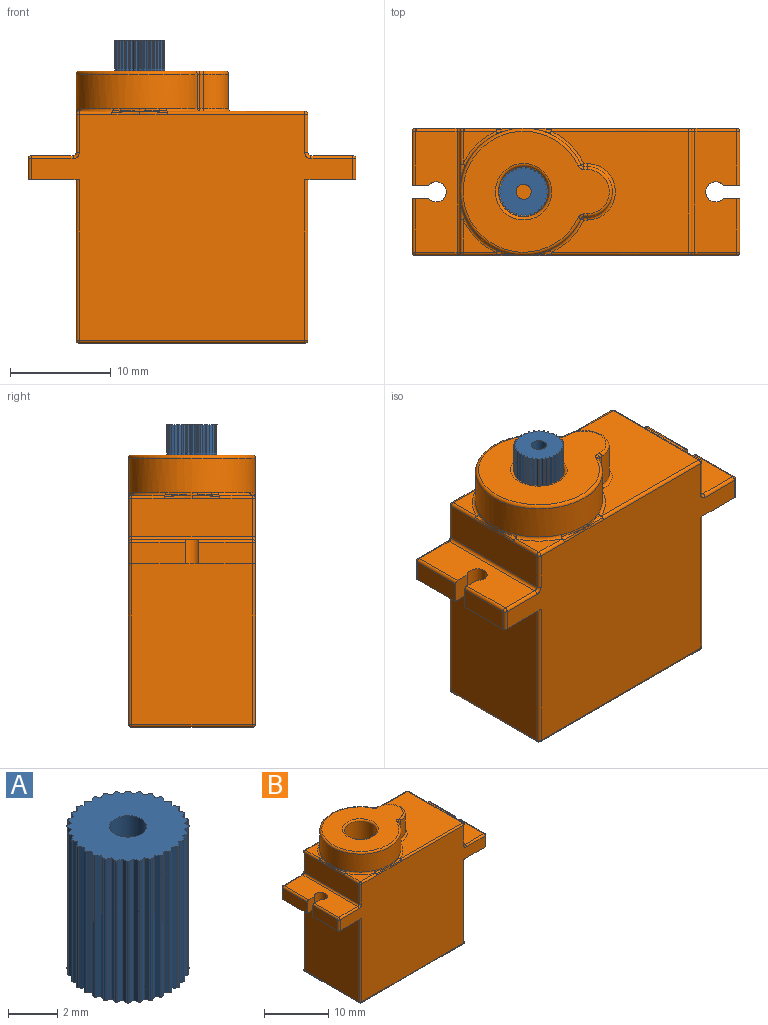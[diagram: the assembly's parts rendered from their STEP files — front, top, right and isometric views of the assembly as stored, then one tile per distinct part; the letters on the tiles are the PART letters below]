
ASSEMBLY  parts=2 mates=1
PART A: 99 faces, bbox 5x5x7 mm
  f0: plane 4.96x4.96mm, normal (0,0,1), area 16.3mm2, adj f1,f2,f3,f4,f5,f6,f7,f8
  f1: plane 7x0.22mm, normal (-0.39,0.92,0), area 1.7mm2, adj f0,f2,f94,f95
  f2: cylinder r=0.08mm len=7mm, axis (0,0,-1), area 0.9mm2, adj f0,f1,f3,f95
  f3: plane 7x0.22mm, normal (-0.93,-0.38,0), area 1.7mm2, adj f0,f2,f4,f95
  f4: plane 7x0.2mm, normal (-0.56,0.83,0), area 1.7mm2, adj f0,f3,f5,f95
  f5: cylinder r=0.08mm len=7mm, axis (0,0,-1), area 0.9mm2, adj f0,f4,f6,f95
  f6: plane 7x0.2mm, normal (-0.83,-0.55,0), area 1.7mm2, adj f0,f5,f7,f95
  f7: plane 7x0.17mm, normal (-0.71,0.7,0), area 1.7mm2, adj f0,f6,f8,f95
  f8: cylinder r=0.08mm len=7mm, axis (0,0,-1), area 0.9mm2, adj f0,f7,f9,f95
  f9: plane 7x0.17mm, normal (-0.71,-0.7,0), area 1.7mm2, adj f0,f8,f10,f95
  f10: plane 7x0.2mm, normal (-0.83,0.55,0), area 1.7mm2, adj f0,f9,f11,f95
  f11: cylinder r=0.08mm len=7mm, axis (0,0,-1), area 0.9mm2, adj f0,f10,f12,f95
  f12: plane 7x0.2mm, normal (-0.56,-0.83,0), area 1.7mm2, adj f0,f11,f13,f95
  f13: plane 7x0.22mm, normal (-0.93,0.38,0), area 1.7mm2, adj f0,f12,f14,f95
  f14: cylinder r=0.08mm len=7mm, axis (0,0,-1), area 0.9mm2, adj f0,f13,f15,f95
  f15: plane 7x0.22mm, normal (-0.39,-0.92,0), area 1.7mm2, adj f0,f14,f16,f95
  f16: plane 7x0.23mm, normal (-0.98,0.19,0), area 1.7mm2, adj f0,f15,f17,f95
  f17: cylinder r=0.08mm len=7mm, axis (0,0,-1), area 0.9mm2, adj f0,f16,f18,f95
  f18: plane 7x0.23mm, normal (-0.2,-0.98,0), area 1.7mm2, adj f0,f17,f19,f95
  f19: plane 7x0.24mm, normal (-1,0,0), area 1.7mm2, adj f0,f18,f20,f95
  f20: cylinder r=0.08mm len=7mm, axis (0,0,-1), area 0.9mm2, adj f0,f19,f21,f95
  f21: plane 7x0.24mm, normal (0,-1,0), area 1.7mm2, adj f0,f20,f22,f95
  f22: plane 7x0.23mm, normal (-0.98,-0.2,0), area 1.7mm2, adj f0,f21,f23,f95
  f23: cylinder r=0.08mm len=7mm, axis (0,0,-1), area 0.9mm2, adj f0,f22,f24,f95
  f24: plane 7x0.23mm, normal (0.19,-0.98,0), area 1.7mm2, adj f0,f23,f25,f95
  f25: plane 7x0.22mm, normal (-0.92,-0.39,0), area 1.7mm2, adj f0,f24,f26,f95
  f26: cylinder r=0.08mm len=7mm, axis (0,0,-1), area 0.9mm2, adj f0,f25,f27,f95
  f27: plane 7x0.22mm, normal (0.38,-0.93,0), area 1.7mm2, adj f0,f26,f28,f95
  f28: plane 7x0.2mm, normal (-0.83,-0.56,0), area 1.7mm2, adj f0,f27,f29,f95
  f29: cylinder r=0.08mm len=7mm, axis (0,0,-1), area 0.9mm2, adj f0,f28,f30,f95
  f30: plane 7x0.2mm, normal (0.55,-0.83,0), area 1.7mm2, adj f0,f29,f31,f95
  f31: plane 7x0.17mm, normal (-0.7,-0.71,0), area 1.7mm2, adj f0,f30,f32,f95
  f32: cylinder r=0.08mm len=7mm, axis (0,0,-1), area 0.9mm2, adj f0,f31,f33,f95
  f33: plane 7x0.17mm, normal (0.7,-0.71,0), area 1.7mm2, adj f0,f32,f34,f95
  f34: plane 7x0.2mm, normal (-0.55,-0.83,0), area 1.7mm2, adj f0,f33,f35,f95
  f35: cylinder r=0.08mm len=7mm, axis (0,0,-1), area 0.9mm2, adj f0,f34,f36,f95
  f36: plane 7x0.2mm, normal (0.83,-0.56,0), area 1.7mm2, adj f0,f35,f37,f95
  f37: plane 7x0.22mm, normal (-0.38,-0.93,0), area 1.7mm2, adj f0,f36,f38,f95
  f38: cylinder r=0.08mm len=7mm, axis (0,0,-1), area 0.9mm2, adj f0,f37,f39,f95
  f39: plane 7x0.22mm, normal (0.92,-0.39,0), area 1.7mm2, adj f0,f38,f40,f95
  f40: plane 7x0.23mm, normal (-0.19,-0.98,0), area 1.7mm2, adj f0,f39,f41,f95
  f41: cylinder r=0.08mm len=7mm, axis (0,0,-1), area 0.9mm2, adj f0,f40,f42,f95
  f42: plane 7x0.23mm, normal (0.98,-0.2,0), area 1.7mm2, adj f0,f41,f43,f95
  f43: plane 7x0.24mm, normal (0,-1,0), area 1.7mm2, adj f0,f42,f44,f95
  f44: cylinder r=0.08mm len=7mm, axis (0,0,-1), area 0.9mm2, adj f0,f43,f45,f95
  f45: plane 7x0.24mm, normal (1,0,0), area 1.7mm2, adj f0,f44,f46,f95
  f46: plane 7x0.23mm, normal (0.2,-0.98,0), area 1.7mm2, adj f0,f45,f47,f95
  f47: cylinder r=0.08mm len=7mm, axis (0,0,-1), area 0.9mm2, adj f0,f46,f48,f95
  f48: plane 7x0.23mm, normal (0.98,0.19,0), area 1.7mm2, adj f0,f47,f49,f95
  f49: plane 7x0.22mm, normal (0.39,-0.92,0), area 1.7mm2, adj f0,f48,f50,f95
  f50: cylinder r=0.08mm len=7mm, axis (0,0,-1), area 0.9mm2, adj f0,f49,f51,f95
  f51: plane 7x0.22mm, normal (0.93,0.38,0), area 1.7mm2, adj f0,f50,f52,f95
  f52: plane 7x0.2mm, normal (0.56,-0.83,0), area 1.7mm2, adj f0,f51,f53,f95
  f53: cylinder r=0.08mm len=7mm, axis (0,0,-1), area 0.9mm2, adj f0,f52,f54,f95
  f54: plane 7x0.2mm, normal (0.83,0.55,0), area 1.7mm2, adj f0,f53,f55,f95
  f55: plane 7x0.17mm, normal (0.71,-0.7,0), area 1.7mm2, adj f0,f54,f56,f95
  f56: cylinder r=0.08mm len=7mm, axis (0,0,-1), area 0.9mm2, adj f0,f55,f57,f95
  f57: plane 7x0.17mm, normal (0.71,0.7,0), area 1.7mm2, adj f0,f56,f58,f95
  f58: plane 7x0.2mm, normal (0.83,-0.55,0), area 1.7mm2, adj f0,f57,f59,f95
  f59: cylinder r=0.08mm len=7mm, axis (0,0,-1), area 0.9mm2, adj f0,f58,f60,f95
  f60: plane 7x0.2mm, normal (0.56,0.83,0), area 1.7mm2, adj f0,f59,f61,f95
  f61: plane 7x0.22mm, normal (0.93,-0.38,0), area 1.7mm2, adj f0,f60,f62,f95
  f62: cylinder r=0.08mm len=7mm, axis (0,0,-1), area 0.9mm2, adj f0,f61,f63,f95
  f63: plane 7x0.22mm, normal (0.39,0.92,0), area 1.7mm2, adj f0,f62,f64,f95
  f64: plane 7x0.23mm, normal (0.98,-0.19,0), area 1.7mm2, adj f0,f63,f65,f95
  f65: cylinder r=0.08mm len=7mm, axis (0,0,-1), area 0.9mm2, adj f0,f64,f66,f95
  f66: plane 7x0.23mm, normal (0.2,0.98,0), area 1.7mm2, adj f0,f65,f67,f95
  f67: plane 7x0.24mm, normal (1,0,0), area 1.7mm2, adj f0,f66,f68,f95
  f68: cylinder r=0.08mm len=7mm, axis (0,0,-1), area 0.9mm2, adj f0,f67,f69,f95
  f69: plane 7x0.24mm, normal (0,1,0), area 1.7mm2, adj f0,f68,f70,f95
  f70: plane 7x0.23mm, normal (0.98,0.2,0), area 1.7mm2, adj f0,f69,f71,f95
  f71: cylinder r=0.08mm len=7mm, axis (0,0,-1), area 0.9mm2, adj f0,f70,f72,f95
  f72: plane 7x0.23mm, normal (-0.19,0.98,0), area 1.7mm2, adj f0,f71,f73,f95
  f73: plane 7x0.22mm, normal (0.92,0.39,0), area 1.7mm2, adj f0,f72,f74,f95
  f74: cylinder r=0.08mm len=7mm, axis (0,0,-1), area 0.9mm2, adj f0,f73,f75,f95
  f75: plane 7x0.22mm, normal (-0.38,0.93,0), area 1.7mm2, adj f0,f74,f76,f95
  f76: plane 7x0.2mm, normal (0.83,0.56,0), area 1.7mm2, adj f0,f75,f77,f95
  f77: cylinder r=0.08mm len=7mm, axis (0,0,-1), area 0.9mm2, adj f0,f76,f78,f95
  f78: plane 7x0.2mm, normal (-0.55,0.83,0), area 1.7mm2, adj f0,f77,f79,f95
  f79: plane 7x0.17mm, normal (0.7,0.71,0), area 1.7mm2, adj f0,f78,f80,f95
  f80: cylinder r=0.08mm len=7mm, axis (0,0,-1), area 0.9mm2, adj f0,f79,f81,f95
  f81: plane 7x0.17mm, normal (-0.7,0.71,0), area 1.7mm2, adj f0,f80,f82,f95
  f82: plane 7x0.2mm, normal (0.55,0.83,0), area 1.7mm2, adj f0,f81,f83,f95
  f83: cylinder r=0.08mm len=7mm, axis (0,0,-1), area 0.9mm2, adj f0,f82,f84,f95
  f84: plane 7x0.2mm, normal (-0.83,0.56,0), area 1.7mm2, adj f0,f83,f85,f95
  f85: plane 7x0.22mm, normal (0.38,0.93,0), area 1.7mm2, adj f0,f84,f86,f95
  f86: cylinder r=0.08mm len=7mm, axis (0,0,-1), area 0.9mm2, adj f0,f85,f87,f95
  f87: plane 7x0.22mm, normal (-0.92,0.39,0), area 1.7mm2, adj f0,f86,f88,f95
  f88: plane 7x0.23mm, normal (0.19,0.98,0), area 1.7mm2, adj f0,f87,f89,f95
  f89: cylinder r=0.08mm len=7mm, axis (0,0,-1), area 0.9mm2, adj f0,f88,f90,f95
  f90: plane 7x0.23mm, normal (-0.98,0.2,0), area 1.7mm2, adj f0,f89,f91,f95
  f91: plane 7x0.24mm, normal (0,1,0), area 1.7mm2, adj f0,f90,f92,f95
  f92: cylinder r=0.08mm len=7mm, axis (0,0,-1), area 0.9mm2, adj f0,f91,f93,f95
  f93: plane 7x0.24mm, normal (-1,0,0), area 1.7mm2, adj f0,f92,f95,f97
  f94: plane 7x0.23mm, normal (-0.98,-0.19,0), area 1.7mm2, adj f0,f1,f95,f98
  f95: plane 4.96x4.96mm, normal (0,0,-1), area 16.3mm2, adj f1,f2,f3,f4,f5,f6,f7,f8
  f96: cylinder r=0.75mm len=7mm, axis (0,0,-1), area 33mm2, adj f0,f95
  f97: plane 7x0.23mm, normal (-0.2,0.98,0), area 1.7mm2, adj f0,f93,f95,f98
  f98: cylinder r=0.08mm len=7mm, axis (0,0,-1), area 0.9mm2, adj f0,f94,f95,f97
PART B: 117 faces, bbox 32.5x13.6x27 mm
  f0: plane 12x3.8mm, normal (-1,0,0), area 45.6mm2, adj f43,f44,f61,f62,f68,f69,f74
  f1: plane 5.35x2.1mm, normal (1,0,0), area 11.2mm2, adj f4,f29,f99,f102
  f2: plane 5.35x2.1mm, normal (-1,0,0), area 11.2mm2, adj f3,f26,f49,f50
  f3: plane 12.6x5.05mm, normal (0,0,-1), area 54.8mm2, adj f2,f9,f10,f11,f17,f25,f26,f27
  f4: plane 12.6x5.05mm, normal (0,0,-1), area 54.8mm2, adj f1,f9,f10,f13,f14,f28,f29,f30
  f5: plane 12x4.15mm, normal (0,0,1), area 45.2mm2, adj f28,f29,f30,f86,f93,f97,f100,f102
  f6: plane 12x4.15mm, normal (0,0,1), area 45.2mm2, adj f25,f26,f27,f46,f50,f51,f56,f61
  f7: plane 13.65x12mm, normal (0,0,1), area 118.8mm2, adj f60,f65,f72,f73,f83,f84,f90,f91
  f8: plane 3.25x3.25mm, normal (0,0,1), area 4mm2, adj f74,f75,f76
  f9: plane 31.9x22.4mm, normal (0,1,0), area 521.9mm2, adj f3,f4,f36,f47,f51,f55,f62,f76
  f10: plane 31.9x22.4mm, normal (0,-1,0), area 521.9mm2, adj f3,f4,f34,f35,f49,f56,f66,f68
  f11: plane 15.9x12mm, normal (-1,0,0), area 190.8mm2, adj f3,f105,f107,f108
  f12: plane 22.4x12mm, normal (0,0,-1), area 268.8mm2, adj f108,f109,f113,f114
  f13: plane 15.9x12mm, normal (1,0,0), area 190.8mm2, adj f4,f110,f114,f116
  f14: plane 5.35x2.1mm, normal (1,0,0), area 11.2mm2, adj f4,f30,f85,f86
  f15: plane 12x3.8mm, normal (1,0,0), area 45.6mm2, adj f91,f92,f96,f97
  f16: plane 3.25x3.25mm, normal (0,0,1), area 4mm2, adj f69,f81,f82
  f17: plane 5.35x2.1mm, normal (-1,0,0), area 11.2mm2, adj f3,f25,f46,f47
  f18: plane 14.5x12mm, normal (0,0,1), area 98mm2, adj f52,f53,f57,f58,f59,f64,f103
  f19: cylinder r=2.5mm len=5mm, axis (0,0,-1), area 26.7mm2, adj f20,f22,f53,f65
  f20: plane 3.4x0.32mm, normal (0,-1,0), area 1.1mm2, adj f19,f59,f71,f72
  f21: cylinder r=2.5mm len=5mm, axis (0,0,-1), area 53.4mm2, adj f103,f104
  f22: plane 3.4x0.32mm, normal (0,1,0), area 1.1mm2, adj f19,f52,f60,f63
  f23: cylinder r=6.3mm len=12.6mm, axis (0,0,-1), area 115.8mm2, adj f31,f32,f38,f39,f41,f58,f63,f71
  f24: plane 4.4x4.4mm, normal (0,0,1), area 15.2mm2, adj f104
  f25: plane 2.4x1.62mm, normal (0,-1,0), area 3.9mm2, adj f3,f6,f17,f27,f46
  f26: plane 2.4x1.62mm, normal (0,1,0), area 3.9mm2, adj f2,f3,f6,f27,f50
  f27: cylinder r=1mm len=2.4mm, axis (0,0,-1), area 11.7mm2, adj f3,f6,f25,f26
  f28: cylinder r=1mm len=2.4mm, axis (0,0,-1), area 11.7mm2, adj f4,f5,f29,f30
  f29: plane 2.4x1.62mm, normal (0,1,0), area 3.9mm2, adj f1,f4,f5,f28,f102
  f30: plane 2.4x1.62mm, normal (0,-1,0), area 3.9mm2, adj f4,f5,f14,f28,f86
  f31: bspline ~2.65x0.57mm, area 0.6mm2, adj f23,f32,f83,f87
  f32: bspline ~2.65x0.57mm, area 0.6mm2, adj f23,f31,f33,f82
  f33: bspline ~2.75x0.48mm, area 0.5mm2, adj f32,f34,f81,f82
  f34: bspline ~2.75x0.3mm, area 0.7mm2, adj f10,f33,f35,f81
  f35: bspline ~2.75x0.3mm, area 0.7mm2, adj f10,f34,f87,f90
  f36: bspline ~2.75x0.3mm, area 0.7mm2, adj f9,f37,f76,f80
  f37: bspline ~2.75x0.48mm, area 0.5mm2, adj f36,f38,f75,f76
  f38: bspline ~2.65x0.57mm, area 0.6mm2, adj f23,f37,f39,f75
  f39: bspline ~2.65x0.57mm, area 0.6mm2, adj f23,f38,f40,f73
  f40: bspline ~2.75x0.48mm, area 0.5mm2, adj f39,f73,f80,f84
  f41: bspline ~2.65x0.57mm, area 0.6mm2, adj f23,f42,f75,f78
  f42: bspline ~2.75x0.48mm, area 0.5mm2, adj f41,f43,f74,f75
  f43: bspline ~2.75x0.3mm, area 0.7mm2, adj f0,f42,f44,f74
  f44: bspline ~2.75x0.3mm, area 0.7mm2, adj f0,f43,f45,f69
  f45: bspline ~2.75x0.48mm, area 0.5mm2, adj f44,f69,f78,f82
  f46: cylinder r=0.3mm len=5.35mm, axis (0,-1,0), area 2.5mm2, adj f6,f17,f25,f48
  f47: cylinder r=0.3mm len=2.1mm, axis (0,0,-1), area 1mm2, adj f3,f9,f17,f48
  f48: sphere r=0.3mm, area 0.2mm2, adj f46,f47,f51
  f49: cylinder r=0.3mm len=2.1mm, axis (0,0,1), area 1mm2, adj f2,f3,f10,f54
  f50: cylinder r=0.3mm len=5.35mm, axis (0,-1,0), area 2.5mm2, adj f2,f6,f26,f54
  f51: cylinder r=0.3mm len=4.15mm, axis (-1,0,0), area 2mm2, adj f6,f9,f48,f55
  f52: cylinder r=0.3mm len=0.32mm, axis (1,0,0), area 0.2mm2, adj f18,f22,f53,f57
  f53: torus R=2.2mm, axis (0,0,1), area 3.5mm2, adj f18,f19,f52,f59
  f54: sphere r=0.3mm, area 0.1mm2, adj f49,f50,f56
  f55: torus R=0.6mm, axis (0,1,0), area 0.3mm2, adj f9,f51,f61,f62
  f56: cylinder r=0.3mm len=4.15mm, axis (1,0,0), area 2mm2, adj f6,f10,f54,f66
  f57: torus R=0.6mm, axis (0,0,1), area 0.2mm2, adj f18,f52,f58,f63
  f58: torus R=6mm, axis (0,0,1), area 15.8mm2, adj f18,f23,f57,f64
  f59: cylinder r=0.3mm len=0.32mm, axis (-1,0,0), area 0.2mm2, adj f18,f20,f53,f64
  f60: cylinder r=0.3mm len=0.32mm, axis (-1,0,0), area 0.2mm2, adj f7,f22,f65,f70
  f61: cylinder r=0.3mm len=12mm, axis (0,1,0), area 5.7mm2, adj f0,f6,f55,f66
  f62: cylinder r=0.3mm len=3.8mm, axis (0,0,-1), area 1.8mm2, adj f0,f9,f55,f67
  f63: cylinder r=0.3mm len=3.4mm, axis (0,0,-1), area 1.2mm2, adj f22,f23,f57,f70
  f64: torus R=0.6mm, axis (0,0,1), area 0.2mm2, adj f18,f58,f59,f71
  f65: torus R=2.8mm, axis (0,0,1), area 3.9mm2, adj f7,f19,f60,f72
  f66: torus R=0.6mm, axis (0,1,0), area 0.3mm2, adj f10,f56,f61,f68
  f67: sphere r=0.3mm, area 0.2mm2, adj f62,f74,f76
  f68: cylinder r=0.3mm len=3.8mm, axis (0,0,1), area 1.8mm2, adj f0,f10,f66,f77
  f69: cylinder r=0.3mm len=3.27mm, axis (0,-1,0), area 1.5mm2, adj f0,f16,f44,f45,f77
  f70: sphere r=0.3mm, area 0.1mm2, adj f60,f63,f73
  f71: cylinder r=0.3mm len=3.4mm, axis (0,0,-1), area 1.2mm2, adj f20,f23,f64,f79
  f72: cylinder r=0.3mm len=0.32mm, axis (1,0,0), area 0.2mm2, adj f7,f20,f65,f79
  f73: torus R=6.6mm, axis (0,0,1), area 2.1mm2, adj f7,f23,f39,f40,f70
  f74: cylinder r=0.3mm len=3.27mm, axis (0,-1,0), area 1.5mm2, adj f0,f8,f42,f43,f67
  f75: torus R=6.6mm, axis (0,0,1), area 2.2mm2, adj f8,f23,f37,f38,f41,f42
  f76: cylinder r=0.3mm len=3.27mm, axis (-1,0,0), area 1.5mm2, adj f8,f9,f36,f37,f67
  f77: sphere r=0.3mm, area 0.1mm2, adj f68,f69,f81
  f78: bspline ~2.65x0.57mm, area 0.6mm2, adj f23,f41,f45,f82
  f79: sphere r=0.3mm, area 0.1mm2, adj f71,f72,f83
  f80: bspline ~2.75x0.3mm, area 0.7mm2, adj f9,f36,f40,f84
  f81: cylinder r=0.3mm len=3.27mm, axis (1,0,0), area 1.5mm2, adj f10,f16,f33,f34,f77
  f82: torus R=6.6mm, axis (0,0,1), area 2.2mm2, adj f16,f23,f32,f33,f45,f78
  f83: torus R=6.6mm, axis (0,0,1), area 2.1mm2, adj f7,f23,f31,f79,f87
  f84: cylinder r=0.3mm len=13.67mm, axis (-1,0,0), area 6.4mm2, adj f7,f9,f40,f80,f88
  f85: cylinder r=0.3mm len=2.1mm, axis (0,0,1), area 1mm2, adj f4,f9,f14,f89
  f86: cylinder r=0.3mm len=5.35mm, axis (0,1,0), area 2.5mm2, adj f5,f14,f30,f89
  f87: bspline ~2.75x0.48mm, area 0.5mm2, adj f31,f35,f83,f90
  f88: sphere r=0.3mm, area 0.1mm2, adj f84,f91,f92
  f89: sphere r=0.3mm, area 0.1mm2, adj f85,f86,f93
  f90: cylinder r=0.3mm len=13.67mm, axis (1,0,0), area 6.4mm2, adj f7,f10,f35,f87,f94
  f91: cylinder r=0.3mm len=12mm, axis (0,1,0), area 5.7mm2, adj f7,f15,f88,f94
  f92: cylinder r=0.3mm len=3.8mm, axis (0,0,1), area 1.8mm2, adj f9,f15,f88,f95
  f93: cylinder r=0.3mm len=4.15mm, axis (-1,0,0), area 2mm2, adj f5,f9,f89,f95
  f94: sphere r=0.3mm, area 0.1mm2, adj f90,f91,f96
  f95: torus R=0.6mm, axis (0,1,0), area 0.3mm2, adj f9,f92,f93,f97
  f96: cylinder r=0.3mm len=3.8mm, axis (0,0,-1), area 1.8mm2, adj f10,f15,f94,f98
  f97: cylinder r=0.3mm len=12mm, axis (0,-1,0), area 5.7mm2, adj f5,f15,f95,f98
  f98: torus R=0.6mm, axis (0,1,0), area 0.3mm2, adj f10,f96,f97,f100
  f99: cylinder r=0.3mm len=2.1mm, axis (0,0,-1), area 1mm2, adj f1,f4,f10,f101
  f100: cylinder r=0.3mm len=4.15mm, axis (1,0,0), area 2mm2, adj f5,f10,f98,f101
  f101: sphere r=0.3mm, area 0.1mm2, adj f99,f100,f102
  f102: cylinder r=0.3mm len=5.35mm, axis (0,1,0), area 2.5mm2, adj f1,f5,f29,f101
  f103: torus R=2.8mm, axis (0,0,1), area 7.7mm2, adj f18,f21
  f104: torus R=2.2mm, axis (0,0,1), area 7.1mm2, adj f21,f24
  f105: cylinder r=0.3mm len=15.9mm, axis (0,0,1), area 7.5mm2, adj f3,f10,f11,f106
  f106: sphere r=0.3mm, area 0.1mm2, adj f105,f108,f109
  f107: cylinder r=0.3mm len=15.9mm, axis (0,0,-1), area 7.5mm2, adj f3,f9,f11,f111
  f108: cylinder r=0.3mm len=12mm, axis (0,1,0), area 5.7mm2, adj f11,f12,f106,f111
  f109: cylinder r=0.3mm len=22.4mm, axis (-1,0,0), area 10.6mm2, adj f10,f12,f106,f112
  f110: cylinder r=0.3mm len=15.9mm, axis (0,0,-1), area 7.5mm2, adj f4,f10,f13,f112
  f111: sphere r=0.3mm, area 0.2mm2, adj f107,f108,f113
  f112: sphere r=0.3mm, area 0.1mm2, adj f109,f110,f114
  f113: cylinder r=0.3mm len=22.4mm, axis (1,0,0), area 10.6mm2, adj f9,f12,f111,f115
  f114: cylinder r=0.3mm len=12mm, axis (0,-1,0), area 5.7mm2, adj f12,f13,f112,f115
  f115: sphere r=0.3mm, area 0.1mm2, adj f113,f114,f116
  f116: cylinder r=0.3mm len=15.9mm, axis (0,0,1), area 7.5mm2, adj f4,f9,f13,f115
PLACE A at identity
PLACE B at identity
MATE fastened B.f21 <-> A.f96  axis (0,0,1) through (-5.2,0,11.5)mm
